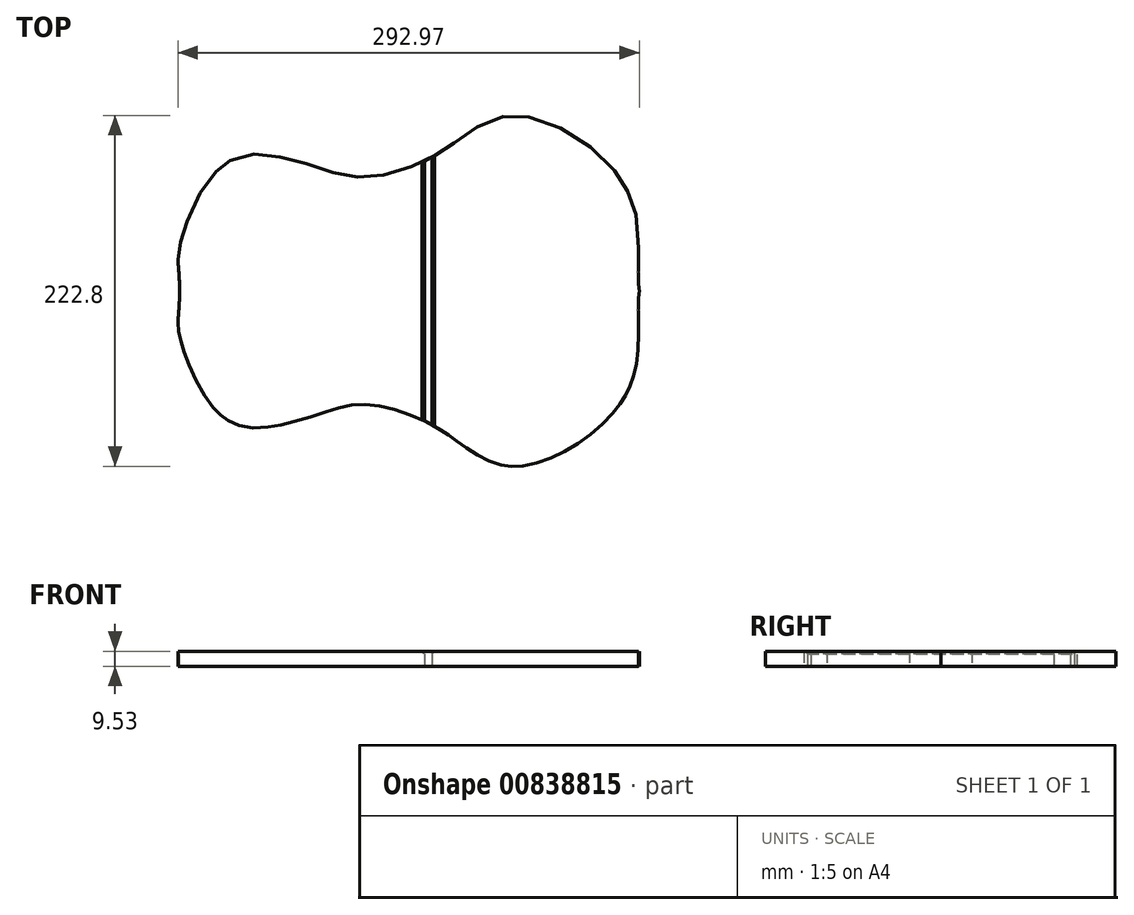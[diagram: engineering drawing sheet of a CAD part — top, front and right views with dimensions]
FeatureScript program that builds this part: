
annotation { "Feature Type Name" : "Feature", "Feature Type Description" : "" }
export const myFeature = defineFeature(function(context is Context, id is Id, definition is map)
    precondition{}
    {
        {
            var Q0;
            Q0=qCreatedBy(makeId("Top.planeOp"),FACE);
            var sketch = newSketch(context, id + "F0", { "sketchPlane" : qUnion([Q0])});
            skFitSpline(sketch, "E0.0", {"points": [v(-120.65, 0) * mm, v(-120.65, 2.86) * mm, v(-120.78, 7.78) * mm, v(-121.14, 13.33) * mm, v(-121.46, 17.64) * mm, v(-121.52, 20.68) * mm, v(-121.36, 23.19) * mm, v(-121.13, 25.21) * mm, v(-120.73, 27.5) * mm, v(-120.15, 30.12) * mm, v(-119.4, 33.04) * mm, v(-118.46, 36.2) * mm, v(-117.36, 39.56) * mm, v(-115.68, 44.24) * mm, v(-113.2, 50.35) * mm, v(-109.68, 57.75) * mm, v(-105.67, 64.87) * mm, v(-102, 70.27) * mm, v(-98.9, 74.1) * mm, v(-96.5, 76.7) * mm, v(-94.47, 78.57) * mm, v(-92.83, 79.9) * mm, v(-91.16, 81.11) * mm, v(-89.05, 82.43) * mm, v(-85.6, 84.16) * mm, v(-81.13, 85.67) * mm, v(-75.54, 86.57) * mm, v(-69.76, 86.7) * mm, v(-63.85, 86.21) * mm, v(-58.88, 85.4) * mm, v(-54.92, 84.57) * mm, v(-51, 83.66) * mm, v(-44.2, 81.86) * mm, v(-36.73, 79.5) * mm, v(-29.7, 77.2) * mm, v(-24.7, 75.6) * mm, v(-19.97, 74.2) * mm, v(-15.38, 73.09) * mm, v(-10.74, 72.3) * mm, v(-5.92, 71.95) * mm, v(-0.77, 72.07) * mm, v(4.85, 72.72) * mm, v(10.87, 73.9) * mm, v(17.2, 75.57) * mm, v(23.74, 77.73) * mm, v(30.39, 80.39) * mm, v(35.92, 83) * mm, v(40.3, 85.33) * mm, v(43.54, 87.2) * mm, v(46.72, 89.17) * mm, v(49.83, 91.23) * mm, v(52.87, 93.34) * mm, v(56.87, 96.16) * mm, v(61.79, 99.64) * mm, v(67.68, 103.5) * mm, v(73.66, 106.8) * mm, v(79.84, 109.33) * mm, v(85.24, 110.64) * mm, v(89.81, 111.12) * mm, v(94.57, 111.17) * mm, v(101, 110.4) * mm, v(109.24, 108.22) * mm, v(117.73, 104.9) * mm, v(126.24, 100.58) * mm, v(134.55, 95.38) * mm, v(142.43, 89.43) * mm, v(149.65, 82.9) * mm, v(154.94, 77.07) * mm, v(158.62, 72.27) * mm, v(161.1, 68.6) * mm, v(163.24, 64.92) * mm, v(165.04, 61.22) * mm, v(166.54, 57.47) * mm, v(168.16, 52.43) * mm, v(169.57, 46.04) * mm, v(170.5, 38.28) * mm, v(170.98, 27.85) * mm, v(170.75, 14.8) * mm, v(170.94, 4.63) * mm, v(171.47, -0.34) * mm]});
            skFitSpline(sketch, "E1.0", {"points": [v(-120.65, 0) * mm, v(-120.65, -2.86) * mm, v(-120.78, -7.78) * mm, v(-121.14, -13.33) * mm, v(-121.46, -17.64) * mm, v(-121.52, -20.68) * mm, v(-121.36, -23.19) * mm, v(-121.13, -25.21) * mm, v(-120.73, -27.5) * mm, v(-120.15, -30.12) * mm, v(-119.4, -33.04) * mm, v(-118.46, -36.2) * mm, v(-117.36, -39.56) * mm, v(-115.68, -44.24) * mm, v(-113.2, -50.35) * mm, v(-109.68, -57.75) * mm, v(-105.67, -64.87) * mm, v(-102, -70.27) * mm, v(-98.9, -74.1) * mm, v(-96.5, -76.7) * mm, v(-94.47, -78.57) * mm, v(-92.83, -79.9) * mm, v(-91.16, -81.11) * mm, v(-89.05, -82.43) * mm, v(-85.6, -84.16) * mm, v(-81.13, -85.67) * mm, v(-75.54, -86.57) * mm, v(-69.76, -86.7) * mm, v(-63.85, -86.21) * mm, v(-58.88, -85.4) * mm, v(-54.92, -84.57) * mm, v(-51, -83.66) * mm, v(-44.2, -81.86) * mm, v(-36.73, -79.5) * mm, v(-29.7, -77.2) * mm, v(-24.7, -75.6) * mm, v(-19.97, -74.2) * mm, v(-15.38, -73.09) * mm, v(-10.74, -72.3) * mm, v(-5.92, -71.95) * mm, v(-0.77, -72.07) * mm, v(4.85, -72.72) * mm, v(10.87, -73.9) * mm, v(17.2, -75.57) * mm, v(23.74, -77.73) * mm, v(30.39, -80.39) * mm, v(35.92, -83) * mm, v(40.3, -85.33) * mm, v(43.54, -87.2) * mm, v(46.72, -89.17) * mm, v(49.83, -91.23) * mm, v(52.87, -93.34) * mm, v(56.87, -96.16) * mm, v(61.79, -99.64) * mm, v(67.68, -103.5) * mm, v(73.66, -106.8) * mm, v(79.84, -109.33) * mm, v(85.24, -110.64) * mm, v(89.81, -111.12) * mm, v(94.57, -111.17) * mm, v(101, -110.4) * mm, v(109.24, -108.22) * mm, v(117.73, -104.9) * mm, v(126.24, -100.58) * mm, v(134.55, -95.38) * mm, v(142.43, -89.43) * mm, v(149.65, -82.9) * mm, v(154.94, -77.07) * mm, v(158.62, -72.27) * mm, v(161.1, -68.6) * mm, v(163.24, -64.92) * mm, v(165.04, -61.22) * mm, v(166.54, -57.47) * mm, v(168.16, -52.43) * mm, v(169.57, -46.04) * mm, v(170.5, -38.28) * mm, v(170.98, -27.85) * mm, v(170.75, -14.8) * mm, v(170.94, -4.63) * mm, v(171.47, 0.34) * mm]});
            skLineSegment(sketch, "E2", {"start": v(-46.04, 82.31) * mm, "end": v(-46.04, -82.31) * mm});
            skLineSegment(sketch, "E3", {"start": v(-41.28, -80.9) * mm, "end": v(-41.28, 80.9) * mm});
            skLineSegment(sketch, "E4", {"start": v(34.92, 82.56) * mm, "end": v(34.93, -82.56) * mm});
            skLineSegment(sketch, "E5", {"start": v(39.69, -85.02) * mm, "end": v(39.69, 85.02) * mm});
            skFitSpline(sketch, "E6.trimOffspring", {"points": [v(-120.65, 0) * mm, v(-120.65, -2.86) * mm, v(-120.78, -7.78) * mm, v(-121.14, -13.33) * mm, v(-121.46, -17.64) * mm, v(-121.52, -20.68) * mm, v(-121.36, -23.19) * mm, v(-121.13, -25.21) * mm, v(-120.73, -27.5) * mm, v(-120.15, -30.12) * mm, v(-119.4, -33.04) * mm, v(-118.46, -36.2) * mm, v(-117.36, -39.56) * mm, v(-115.68, -44.24) * mm, v(-113.2, -50.35) * mm, v(-109.68, -57.75) * mm, v(-105.67, -64.87) * mm, v(-102, -70.27) * mm, v(-98.9, -74.1) * mm, v(-96.5, -76.7) * mm, v(-94.47, -78.57) * mm, v(-92.83, -79.9) * mm, v(-91.16, -81.11) * mm, v(-89.05, -82.43) * mm, v(-85.6, -84.16) * mm, v(-81.13, -85.67) * mm, v(-75.54, -86.57) * mm, v(-69.76, -86.7) * mm, v(-63.85, -86.21) * mm, v(-58.88, -85.4) * mm, v(-54.92, -84.57) * mm, v(-51, -83.66) * mm, v(-44.2, -81.86) * mm, v(-36.73, -79.5) * mm, v(-29.7, -77.2) * mm, v(-24.7, -75.6) * mm, v(-19.97, -74.2) * mm, v(-15.38, -73.09) * mm, v(-10.74, -72.3) * mm, v(-5.92, -71.95) * mm, v(-0.77, -72.07) * mm, v(4.85, -72.72) * mm, v(10.87, -73.9) * mm, v(17.2, -75.57) * mm, v(23.74, -77.73) * mm, v(30.39, -80.39) * mm, v(35.92, -83) * mm, v(40.3, -85.33) * mm, v(43.54, -87.2) * mm, v(46.72, -89.17) * mm, v(49.83, -91.23) * mm, v(52.87, -93.34) * mm, v(56.87, -96.16) * mm, v(61.79, -99.64) * mm, v(67.68, -103.5) * mm, v(73.66, -106.8) * mm, v(79.84, -109.33) * mm, v(85.24, -110.64) * mm, v(89.81, -111.12) * mm, v(94.57, -111.17) * mm, v(101, -110.4) * mm, v(109.24, -108.22) * mm, v(117.73, -104.9) * mm, v(126.24, -100.58) * mm, v(134.55, -95.38) * mm, v(142.43, -89.43) * mm, v(149.65, -82.9) * mm, v(154.94, -77.07) * mm, v(158.62, -72.27) * mm, v(161.1, -68.6) * mm, v(163.24, -64.92) * mm, v(165.04, -61.22) * mm, v(166.54, -57.47) * mm, v(168.16, -52.43) * mm, v(169.57, -46.04) * mm, v(170.5, -38.28) * mm, v(170.98, -27.85) * mm, v(170.75, -14.8) * mm, v(170.94, -4.63) * mm, v(171.47, 0.34) * mm]});
            skFitSpline(sketch, "E7.trimOffspring", {"points": [v(-120.65, 0) * mm, v(-120.65, 2.86) * mm, v(-120.78, 7.78) * mm, v(-121.14, 13.33) * mm, v(-121.46, 17.64) * mm, v(-121.52, 20.68) * mm, v(-121.36, 23.19) * mm, v(-121.13, 25.21) * mm, v(-120.73, 27.5) * mm, v(-120.15, 30.12) * mm, v(-119.4, 33.04) * mm, v(-118.46, 36.2) * mm, v(-117.36, 39.56) * mm, v(-115.68, 44.24) * mm, v(-113.2, 50.35) * mm, v(-109.68, 57.75) * mm, v(-105.67, 64.87) * mm, v(-102, 70.27) * mm, v(-98.9, 74.1) * mm, v(-96.5, 76.7) * mm, v(-94.47, 78.57) * mm, v(-92.83, 79.9) * mm, v(-91.16, 81.11) * mm, v(-89.05, 82.43) * mm, v(-85.6, 84.16) * mm, v(-81.13, 85.67) * mm, v(-75.54, 86.57) * mm, v(-69.76, 86.7) * mm, v(-63.85, 86.21) * mm, v(-58.88, 85.4) * mm, v(-54.92, 84.57) * mm, v(-51, 83.66) * mm, v(-44.2, 81.86) * mm, v(-36.73, 79.5) * mm, v(-29.7, 77.2) * mm, v(-24.7, 75.6) * mm, v(-19.97, 74.2) * mm, v(-15.38, 73.09) * mm, v(-10.74, 72.3) * mm, v(-5.92, 71.95) * mm, v(-0.77, 72.07) * mm, v(4.85, 72.72) * mm, v(10.87, 73.9) * mm, v(17.2, 75.57) * mm, v(23.74, 77.73) * mm, v(30.39, 80.39) * mm, v(35.92, 83) * mm, v(40.3, 85.33) * mm, v(43.54, 87.2) * mm, v(46.72, 89.17) * mm, v(49.83, 91.23) * mm, v(52.87, 93.34) * mm, v(56.87, 96.16) * mm, v(61.79, 99.64) * mm, v(67.68, 103.5) * mm, v(73.66, 106.8) * mm, v(79.84, 109.33) * mm, v(85.24, 110.64) * mm, v(89.81, 111.12) * mm, v(94.57, 111.17) * mm, v(101, 110.4) * mm, v(109.24, 108.22) * mm, v(117.73, 104.9) * mm, v(126.24, 100.58) * mm, v(134.55, 95.38) * mm, v(142.43, 89.43) * mm, v(149.65, 82.9) * mm, v(154.94, 77.07) * mm, v(158.62, 72.27) * mm, v(161.1, 68.6) * mm, v(163.24, 64.92) * mm, v(165.04, 61.22) * mm, v(166.54, 57.47) * mm, v(168.16, 52.43) * mm, v(169.57, 46.04) * mm, v(170.5, 38.28) * mm, v(170.98, 27.85) * mm, v(170.75, 14.8) * mm, v(170.94, 4.63) * mm, v(171.47, -0.34) * mm]});
            skFitSpline(sketch, "E8.0", {"points": [v(-120.65, 0.38) * mm, v(-120.65, 3.24) * mm, v(-120.78, 8.15) * mm, v(-121.14, 13.71) * mm, v(-121.46, 18.02) * mm, v(-121.52, 21.06) * mm, v(-121.36, 23.56) * mm, v(-121.13, 25.6) * mm, v(-120.73, 27.87) * mm, v(-120.15, 30.5) * mm, v(-119.4, 33.42) * mm, v(-118.46, 36.59) * mm, v(-117.36, 39.94) * mm, v(-115.68, 44.62) * mm, v(-113.2, 50.73) * mm, v(-109.68, 58.12) * mm, v(-105.67, 65.24) * mm, v(-102, 70.65) * mm, v(-98.9, 74.49) * mm, v(-96.5, 77.07) * mm, v(-94.47, 78.95) * mm, v(-92.83, 80.28) * mm, v(-91.16, 81.5) * mm, v(-89.05, 82.81) * mm, v(-85.6, 84.54) * mm, v(-81.13, 86.05) * mm, v(-75.54, 86.95) * mm, v(-69.76, 87.09) * mm, v(-63.85, 86.6) * mm, v(-58.88, 85.77) * mm, v(-54.92, 84.95) * mm, v(-51, 84.04) * mm, v(-44.2, 82.23) * mm, v(-36.73, 79.88) * mm, v(-29.7, 77.58) * mm, v(-24.7, 75.98) * mm, v(-19.97, 74.59) * mm, v(-15.38, 73.47) * mm, v(-10.74, 72.69) * mm, v(-5.92, 72.33) * mm, v(-0.77, 72.45) * mm, v(4.85, 73.1) * mm, v(10.87, 74.27) * mm, v(17.2, 75.94) * mm, v(23.74, 78.11) * mm, v(30.39, 80.77) * mm, v(35.92, 83.38) * mm, v(40.3, 85.7) * mm, v(43.54, 87.57) * mm, v(46.72, 89.55) * mm, v(49.83, 91.61) * mm, v(52.87, 93.72) * mm, v(56.87, 96.54) * mm, v(61.79, 100.02) * mm, v(67.68, 103.87) * mm, v(73.66, 107.17) * mm, v(79.84, 109.7) * mm, v(85.24, 111.02) * mm, v(89.81, 111.5) * mm, v(94.57, 111.55) * mm, v(101, 110.77) * mm, v(109.24, 108.6) * mm, v(117.73, 105.29) * mm, v(126.24, 100.96) * mm, v(134.55, 95.76) * mm, v(142.43, 89.81) * mm, v(149.65, 83.27) * mm, v(154.94, 77.45) * mm, v(158.62, 72.64) * mm, v(161.1, 68.99) * mm, v(163.24, 65.3) * mm, v(165.04, 61.6) * mm, v(166.54, 57.85) * mm, v(168.16, 52.8) * mm, v(169.57, 46.42) * mm, v(170.5, 38.65) * mm, v(170.98, 28.22) * mm, v(170.75, 15.18) * mm, v(170.94, 5) * mm, v(171.47, 0.04) * mm]});
            skLineSegment(sketch, "E9", {"start": v(100.01, 110.77) * mm, "end": v(100.01, -110) * mm});
            skLineSegment(sketch, "E10", {"start": v(104.78, -108.98) * mm, "end": v(104.78, 109.73) * mm});
            skFitSpline(sketch, "E11.trimOffspring", {"points": [v(-120.65, 0.38) * mm, v(-120.65, -2.48) * mm, v(-120.78, -7.4) * mm, v(-121.14, -12.95) * mm, v(-121.46, -17.26) * mm, v(-121.52, -20.3) * mm, v(-121.36, -22.8) * mm, v(-121.13, -24.84) * mm, v(-120.73, -27.12) * mm, v(-120.15, -29.75) * mm, v(-119.4, -32.67) * mm, v(-118.46, -35.83) * mm, v(-117.36, -39.19) * mm, v(-115.68, -43.86) * mm, v(-113.2, -49.97) * mm, v(-109.68, -57.37) * mm, v(-105.67, -64.49) * mm, v(-102, -69.9) * mm, v(-98.9, -73.73) * mm, v(-96.5, -76.32) * mm, v(-94.47, -78.2) * mm, v(-92.83, -79.52) * mm, v(-91.16, -80.73) * mm, v(-89.05, -82.05) * mm, v(-85.6, -83.79) * mm, v(-81.13, -85.29) * mm, v(-75.54, -86.2) * mm, v(-69.76, -86.33) * mm, v(-63.85, -85.83) * mm, v(-58.88, -85.01) * mm, v(-54.92, -84.2) * mm, v(-51, -83.28) * mm, v(-44.2, -81.48) * mm, v(-36.73, -79.12) * mm, v(-29.7, -76.82) * mm, v(-24.7, -75.22) * mm, v(-19.97, -73.83) * mm, v(-15.38, -72.7) * mm, v(-10.74, -71.93) * mm, v(-5.92, -71.57) * mm, v(-0.77, -71.7) * mm, v(4.85, -72.34) * mm, v(10.87, -73.51) * mm, v(17.2, -75.19) * mm, v(23.74, -77.36) * mm, v(30.39, -80) * mm, v(35.92, -82.62) * mm, v(40.3, -84.95) * mm, v(43.54, -86.81) * mm, v(46.72, -88.8) * mm, v(49.83, -90.86) * mm, v(52.87, -92.96) * mm, v(56.87, -95.78) * mm, v(61.79, -99.26) * mm, v(67.68, -103.12) * mm, v(73.66, -106.42) * mm, v(79.84, -108.95) * mm, v(85.24, -110.26) * mm, v(89.81, -110.74) * mm, v(94.57, -110.79) * mm, v(101, -110.02) * mm, v(109.24, -107.84) * mm, v(117.73, -104.53) * mm, v(126.24, -100.2) * mm, v(134.55, -95) * mm, v(142.43, -89.06) * mm, v(149.65, -82.52) * mm, v(154.94, -76.7) * mm, v(158.62, -71.89) * mm, v(161.1, -68.23) * mm, v(163.24, -64.54) * mm, v(165.04, -60.84) * mm, v(166.54, -57.09) * mm, v(168.16, -52.05) * mm, v(169.57, -45.66) * mm, v(170.5, -37.9) * mm, v(170.98, -27.47) * mm, v(170.75, -14.42) * mm, v(170.94, -4.25) * mm, v(171.47, 0.72) * mm]});
            skSolve(sketch);
        }
        {
            var Q0;
            Q0=qSketchRegion(id+"F0",true);
            extrude(context, id + "F1", {"entities" : qUnion([Q0]), "depth" : 9.52 * mm, "offsetDistance" : 25.4 * mm});
        }
        {
            var Q0;
            Q0=makeQuery(id+"F1.opExtrude","CAP_EDGE",EDGE,{"disambiguationData":[OSD([sQuery(id+"F0.wireOp",EDGE,"E3")])],"isStart":false});
            var Q1;
            Q1=makeQuery(id+"F1.opExtrude","CAP_EDGE",EDGE,{"disambiguationData":[OSD([sQuery(id+"F0.wireOp",EDGE,"E2")])],"isStart":false});
            var Q2;
            Q2=makeQuery(id+"F1.opExtrude","CAP_EDGE",EDGE,{"disambiguationData":[OSD([sQuery(id+"F0.wireOp",EDGE,"E5")])],"isStart":false});
            var Q3;
            Q3=makeQuery(id+"F1.opExtrude","CAP_EDGE",EDGE,{"disambiguationData":[OSD([sQuery(id+"F0.wireOp",EDGE,"E4")])],"isStart":false});
            var Q4;
            Q4=makeQuery(id+"F1.opExtrude","CAP_EDGE",EDGE,{"disambiguationData":[OSD([sQuery(id+"F0.wireOp",EDGE,"E9")])],"isStart":false});
            var Q5;
            Q5=makeQuery(id+"F1.opExtrude","CAP_EDGE",EDGE,{"disambiguationData":[OSD([sQuery(id+"F0.wireOp",EDGE,"E10")])],"isStart":false});
            chamfer(context, id + "F2", {"entities" : qUnion([Q0, Q1, Q2, Q3, Q4, Q5]), "width" : 1.59 * mm, "tangentPropagation" : true});
        }
    });
